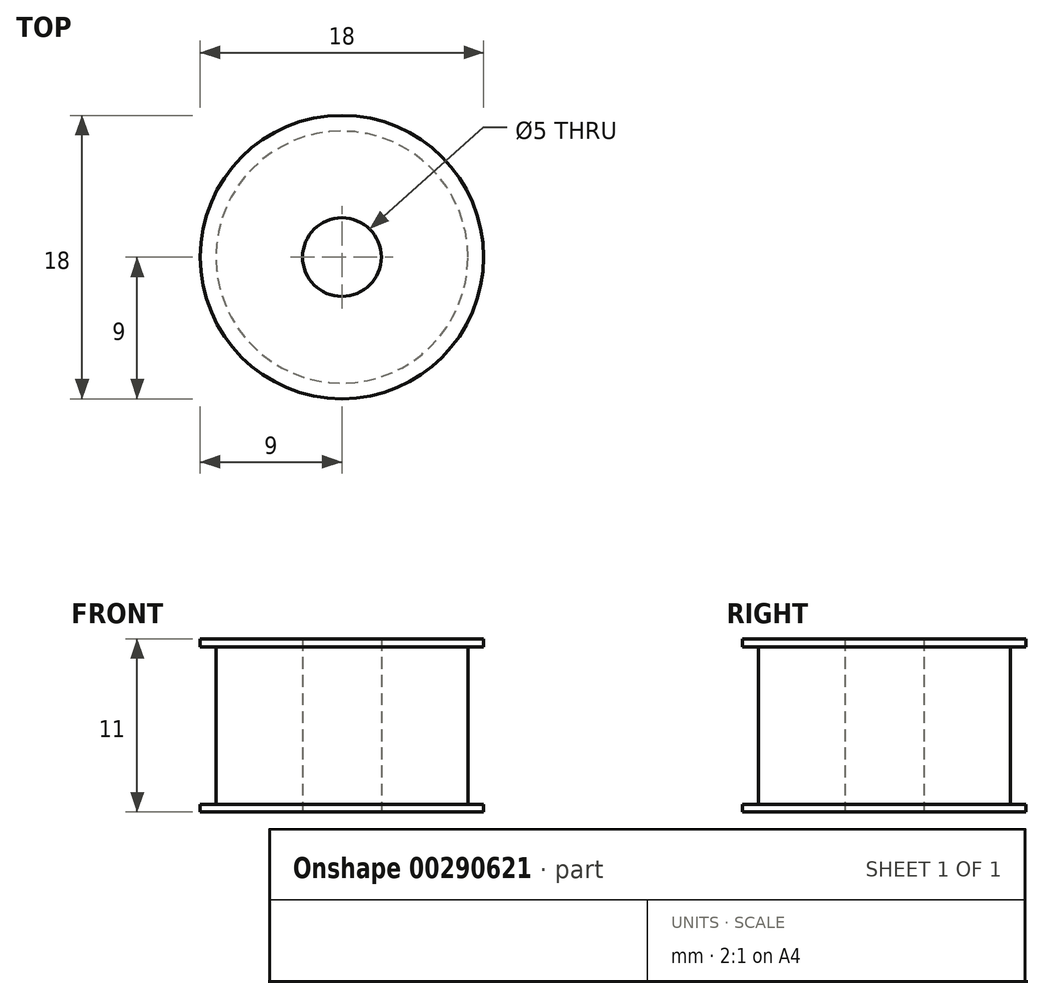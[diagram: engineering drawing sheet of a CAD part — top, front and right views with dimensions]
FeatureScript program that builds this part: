
annotation { "Feature Type Name" : "Feature", "Feature Type Description" : "" }
export const myFeature = defineFeature(function(context is Context, id is Id, definition is map)
    precondition{}
    {
        {
            var Q0;
            Q0=qCreatedBy(makeId("Top.planeOp"),FACE);
            var sketch = newSketch(context, id + "F0", { "sketchPlane" : qUnion([Q0])});
            skCircle(sketch, "E0", {"center": v(0, 0) * mm, "radius": 9 * mm});
            skCircle(sketch, "E1", {"center": v(0, 0) * mm, "radius": 8 * mm});
            skCircle(sketch, "E2", {"center": v(0, 0) * mm, "radius": 2.5 * mm});
            skSolve(sketch);
        }
        {
            var Q0;
            Q0=makeQuery(id+"F0.imprint","IMPRINT",FACE,{"disambiguationData":[TD([[makeQuery(id+"F0.imprint","IMPRINT",EDGE,{"derivedFrom":sQuery(id+"F0.wireOp",EDGE,"E1")}),1.0]])]});
            extrude(context, id + "F1", {"entities" : qUnion([Q0]), "depth" : 11 * mm});
        }
        {
            var Q0;
            Q0=makeQuery(id+"F0.imprint","IMPRINT",FACE,{"disambiguationData":[TD([[makeQuery(id+"F0.imprint","IMPRINT",EDGE,{"derivedFrom":sQuery(id+"F0.wireOp",EDGE,"E0")}),1.0]])]});
            extrude(context, id + "F2", {"entities" : qUnion([Q0]), "operationType" : NewBodyOperationType.ADD, "depth" : 0.5 * mm});
        }
        {
            var Q0;
            Q0=makeQuery(id+"F0.imprint","IMPRINT",FACE,{"disambiguationData":[TD([[makeQuery(id+"F0.imprint","IMPRINT",EDGE,{"derivedFrom":sQuery(id+"F0.wireOp",EDGE,"E0")}),1.0]])]});
            extrude(context, id + "F3", {"entities" : qUnion([Q0]), "operationType" : NewBodyOperationType.ADD, "depth" : 11 * mm, "hasSecondDirection" : true, "secondDirectionOppositeDirection" : false, "secondDirectionDepth" : 10.5 * mm});
        }
    });
